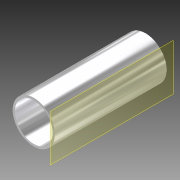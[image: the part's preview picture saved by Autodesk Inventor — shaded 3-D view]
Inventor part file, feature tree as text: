
AUTODESK INVENTOR PART (.ipt)
format: ipt  version: 2011 (Build 150239000, 239)  size: 92,160 bytes
history: native  units: in
note: dims shown in document units (in); Inventor stores cm internally (conversion verified against a paired STEP export)
features: sketch x3, extrude x2, plane x1
ambient origin geometry x8: Origin, YZ Plane, XZ Plane, XY Plane, X Axis, Y Axis, Z Axis, Center Point
bodies: Solid1 (feature_tree)
feature tree (6):
  extrude  "Extrusion1"  Depth=5.502in TaperAngle=0.0deg
  plane  "Work Plane1"
  sketch  "Sketch2"  dims[d3=1.5in d14=1.862in]
  extrude  "Extrusion2"  Depth=1.862in
  sketch  "Sketch1"  dims[d0=2.08in d1=5.502in d2=0.0in]
  sketch  "Sketch3"  dims[d15=1.0in d16=0.0in]
